# Revit family: QF_ELECTROLUXPROFESSIONAL_1LSN7U_WB6-35_E
name_source: partatom
category: Attrezzature speciali
units: mm (PartAtom-declared; Revit-internal decimal feet)

## family parameters
Basato su piano di lavoro = No
Condiviso = No
Punto di calcolo locali = No
Quota connettore circolare = Usa diametro
Sempre verticale = Sì
Taglio con vuoti quando caricato = No
Tipo di parte = Normale

## types (67) — shared parameters
Cold Water Maximum Pressure = 0.00 psi
Cold Water Minimum Pressure = 0.00 psi
Cold Water Size = 1"
Conn Conduit = Sì
Depth Actual = 1030 mm  [stored 3.37927 ft]
Electrical Remarks = 400 V/3N ph/50/60 Hz
Height Actual = 1620 mm
Hot Water Consumption = 0 GPM
Hot Water Maximum Pressure = 0.00 psi
Hot Water Minimum Pressure = 0.00 psi
Hot Water Size = 1"
Hot Water Temperature = -460 °F
Indirect Waste Size = 1"
Latent Heat Output = 0.0
Length Actual = 1270 mm  [stored 4.16667 ft]
Max Overcurrent Protection = 0 A
Min Ckt Ampacity = 0 A
Modello = WB6-35
Phase = 3
Produttore = Electrolux Professional
Sensible Heat Output = 0.0
URL = www.electroluxprofessional.com
Weight = 770
Weight in Pounds = 55.1
zero-valued in all types: Cold Water Connection Height, Gas KW, Hot Water Connection Height, Indirect Waste Connection Height, Prospetto di default, Steam Pounds per Hour

## per-type parameters (varying)
| type | Descrizione | Volts | Watts |
| 9890230074 | WASHER WB6-35 350L 2DOORS LEFT/LEFT EL. 380-415/50/60/3 COMPASS PRO 2xWATER 13xLIQ. SILVER EXP. | 415 V | 28800 W |
| 9890230044 | WASHER WB6-35 350L 2DOORS RIGHT/LEFT EL. 380-415/50/60/3 2xCOMPASS PRO 2xWATER 13xLIQ. SILVER ALARM | 415 V | 28800 W |
| 9890230034 | WASHER WB6-35 350L 2DOORS RIGHT/RIGHT EL. 380-415/50/60/3 COMPASS PRO 3xWATER 13xLIQ.+POWDER SILVER EXP. | 415 V | 28800 W |
| 9890230014 | WASHER WB6-35 350L 2DOORS RIGHT/RIGHT EL. 230/50/60/3 2xCOMPASS PRO 2xWATER 13xLIQ. SILVER AIDO TAP ALARM EXP. | 230 V | 28800 W |
| 9890230061 | WASHER WB6-35 350L 2DOORS RIGHT/RIGHT EL. 380-415/50/60/3 2xCOMPASS PRO 2xWATER 13xLIQ.+POWDER SST AIDO ALARM EXP. | 415 V | 31500 W |
| 9890230051 | WASHER WB6-35 350L 2DOORS RIGHT/RIGHT EL. 380-415/50/60/3 COMPASS PRO 2xWATER 13xLIQ. SILVER TAP ALARM EXP. | 415 V | 28800 W |
| 9890230041 | WASHER WB6-35 350L 2DOORS LEFT/RIGHT EL. 380-415/50/60/3 COMPASS PRO 3xWATER 13xLIQ.+POWDER SILVER EXP. | 415 V | 28800 W |
| 9890230031 | WASHER WB6-35 350L 2DOORS RIGHT/RIGHT EL. 380-415/50/60/3 2xCOMPASS PRO 2xWATER 13xLIQ. SILVER AIDO | 415 V | 28800 W |
| 9890230021 | WASHER WB6-35 350L 2DOORS RIGHT/RIGHT EL. 380-415/50/60/3 2xCOMPASS PRO 2xWATER 13xLIQ. SILVER EXP. | 415 V | 28800 W |
| 9890230011 | WASHER WB6-35 350L 2DOORS RIGHT/LEFT EL. 380-415/50/60/3 COMPASS PRO 2xWATER 13xLIQ. SILVER | 415 V | 28800 W |
| 9893230007 | WASHER WB6-35 350L 2DOORS RIGHT/RIGHT EL. 480/50/60/3 COMPASS PRO 2xWATER 13xLIQ. SILVER TAP ALARM EXP. ETL | 480 V | 28800 W |
| 9891230006 | WASHER WB6-35 350L 1DOOR RIGHT EL. 380-415/50/60/3 COMPASS PRO 2xWATER 13xLIQ. SILVER | 415 V | 28800 W |
| 9890230059 | WASHER WB6-35 350L 2DOORS LEFT/LEFT EL. 380-415/50/60/3 2xCOMPASS PRO 2xWATER 13xLIQ. SILVER TAP ALARM EXP. | 415 V | 28800 W |
| 9890230049 | WASHER WB6-35 350L 2DOORS LEFT/RIGHT EL. 380-415/50/60/3 2xCOMPASS PRO 2xWATER 13xLIQ. SILVER AIDO IWS ALARM | 415 V | 28800 W |
| 9890230039 | WASHER WB6-35 350L 2DOORS RIGHT/RIGHT EL. 380-415/50/60/3 2xCOMPASS PRO 2xWATER 13xLIQ. SILVER TAP ALARM | 415 V | 28800 W |
| 9890230029 | WASHER WB6-35 350L 2DOORS LEFT/RIGHT EL. 380-415/50/60/3 COMPASS PRO 3xWATER 13xLIQ. SILVER | 415 V | 28800 W |
| 9890230019 | WASHER WB6-35 350L 2DOORS RIGHT/RIGHT EL. 380-415/50/60/3 COMPASS PRO 2xWATER 13xLIQ. SILVER ALARM EXP. | 415 V | 28800 W |
| 9890230009 | WASHER WB6-35 350L 2DOORS RIGHT/RIGHT EL. 380-415/50/60/3 2xCOMPASS PRO 2xWATER 13xLIQ. SILVER IWS ALARM EXP. | 415 V | 28800 W |
| 9891230001 | WASHER WB6-35 350L 1DOOR RIGHT EL. 380-415/50/60/3 COMPASS PRO 2xWATER 13xLIQ.+POWDER SILVER | 415 V | 28800 W |
| 9893230002 | WASHER WB6-35 350L 2DOORS RIGHT/RIGHT EL. 208-240/50/60/3 2xCOMPASS PRO 3xWATER 13xLIQ. SILVER AIDO ALARM EXP. ETL | 240 V | 28800 W |
| 9890230052 | WASHER WB6-35 350L 2DOORS RIGHT/RIGHT EL. 380-415/50/60/3 2xCOMPASS PRO 2xWATER 13xLIQ.+POWDER SST ALARM EXP. | 415 V | 28800 W |
| 9890230022 | WASHER WB6-35 350L 2DOORS RIGHT/RIGHT EL. 380-415/50/60/3 2xCOMPASS PRO 2xWATER 13xLIQ.+POWDER SILVER EXP. | 415 V | 28800 W |
| 9890230012 | WASHER WB6-35 350L 2DOORS LEFT/RIGHT EL. 380-415/50/60/3 COMPASS PRO 2xWATER 13xLIQ. SILVER | 415 V | 28800 W |
| 9890230082 | WASHER WB6-35 350L 2DOORS RIGHT/RIGHT EL. 380-415/50/60/3 2xCOMPASS PRO 2xWATER 13xLIQ. SILVER ALARM BMP EXP. | 415 V | 28800 W |
| 9893230001 | WASHER WB6-35 350L 2DOORS RIGHT/RIGHT NO HEATING 208-240/50/60/3 COMPASS PRO 2xWATER 13xLIQ.+POWDER SST ALARM EXP. ETL | 240 V | 6400 W |
| 9890230067 | WASHER WB6-35 350L 2DOORS RIGHT/RIGHT EL. 380-415/50/60/3 2xCOMPASS PRO 2xWATER 13xLIQ. SILVER IWS EXP. | 415 V | 28800 W |
| 9890230057 | WASHER WB6-35 350L 2DOORS RIGHT/RIGHT EL. 380-415/50/60/3 COMPASS PRO 2xWATER 13xLIQ.+POWDER SILVER ALARM EXP. | 415 V | 28800 W |
| 9890230047 | WASHER WB6-35 350L 2DOORS RIGHT/RIGHT EL. 380-415/50/60/3 2xCOMPASS PRO 3xWATER 13xLIQ. SILVER ALARM | 415 V | 28800 W |
| 9890230027 | WASHER WB6-35 350L 2DOORS RIGHT/RIGHT EL. 380-415/50/60/3 COMPASS PRO 2xWATER 13xLIQ.+POWDER SST EXP. | 415 V | 28800 W |
| 9890230017 | WASHER WB6-35 350L 2DOORS LEFT/RIGHT EL. 380-415/50/60/3 COMPASS PRO 2xWATER 13xLIQ. SILVER ALARM | 415 V | 28800 W |
| 9890230007 | WASHER WB6-35 350L 2DOORS RIGHT/RIGHT EL. 380-415/50/60/3 2xCOMPASS PRO 2xWATER 13xLIQ. SILVER | 415 V | 28800 W |
| 9890230070 | WASHER WB6-35 350L 2DOORS RIGHT/RIGHT EL. 380-415/50/60/3 COMPASS PRO 2xWATER 13xLIQ.+POWDER SILVER EXP. | 415 V | 28800 W |
| 9890230060 | WASHER WB6-35 350L 2DOORS RIGHT/RIGHT EL. 380-415/50/60/3 2xCOMPASS PRO 2xWATER 13xLIQ. SILVER AIDO ALARM | 415 V | 31500 W |
| 9890230040 | WASHER WB6-35 350L 2DOORS LEFT/RIGHT EL. 380-415/50/60/3 COMPASS PRO 2xWATER 13xLIQ.+POWDER SILVER BMP | 415 V | 28800 W |
| 9890230030 | WASHER WB6-35 350L 2DOORS RIGHT/RIGHT EL. 380-415/50/60/3 COMPASS PRO 2xWATER 13xLIQ. SILVER IWS | 415 V | 28800 W |
| 9890230020 | WASHER WB6-35 350L 2DOORS RIGHT/RIGHT EL. 380-415/50/60/3 2xCOMPASS PRO 2xWATER 13xLIQ.+POWDER SILVER AIDO | 415 V | 28800 W |
| 9890230010 | WASHER WB6-35 350L 2DOORS RIGHT/RIGHT EL. 380-415/50/60/3 2xCOMPASS PRO 2xWATER 13xLIQ. SILVER AIDO IWS TAP ALARM EXP. | 415 V | 28800 W |
| 9893230004 | WASHER WB6-35 350L 2DOORS RIGHT/RIGHT EL. 208-240/50/60/3 COMPASS PRO 2xWATER 13xLIQ.+POWDER SILVER ALARM EXP. ETL | 240 V | 28800 W |
| 9890230078 | WASHER WB6-35 350L 2DOORS RIGHT/RIGHT EL. 380-415/50/60/3 2xCOMPASS PRO 2xWATER 13xLIQ. SILVER AIDO IWS TAP ALARM EXP. | 415 V | 28800 W |
| 9890230048 | WASHER WB6-35 350L 2DOORS LEFT/RIGHT EL. 380-415/50/60/3 COMPASS PRO 2xWATER 13xLIQ. SILVER EXP. | 415 V | 28800 W |
| 9890230038 | WASHER WB6-35 350L 2DOORS RIGHT/RIGHT EL. 380-415/50/60/3 2xCOMPASS PRO 2xWATER 13xLIQ.+POWDER SILVER | 415 V | 28800 W |
| 9890230028 | WASHER WB6-35 350L 2DOORS RIGHT/RIGHT EL. 380-415/50/60/3 COMPASS PRO 2xWATER 13xLIQ. SST IWS TAP ALARM EXP. | 415 V | 28800 W |
| 9890230018 | WASHER WB6-35 350L 2DOORS RIGHT/RIGHT EL. 380-415/50/60/3 2xCOMPASS PRO 2xWATER 13xLIQ. SILVER AIDO TAP ALARM | 415 V | 28800 W |
| 9890230008 | WASHER WB6-35 350L 2DOORS RIGHT/RIGHT EL. 380-415/50/60/3 COMPASS PRO 2xWATER 13xLIQ. SILVER | 415 V | 28800 W |
| 9890230080 | WASHER WB6-35 350L 2DOORS RIGHT/LEFT EL. 380-415/50/60/3 COMPASS PRO 2xWATER 13xLIQ. SILVER EXP. | 415 V | 28800 W |
| 9890230075 | WASHER WB6-35 350L 2DOORS RIGHT/RIGHT EL. 380-415/50/60/3 2xCOMPASS PRO 3xWATER 13xLIQ.+POWDER SILVER AIDO TAP ALARM | 415 V | 28800 W |
| 9893230003 | WASHER WB6-35 350L 2DOORS RIGHT/RIGHT NO HEATING 208-240/50/60/3 COMPASS PRO 2xWATER 13xLIQ.+POWDER SILVER ALARM EXP. ET | 240 V | 6400 W |
| 9890230065 | WASHER WB6-35 350L 2DOORS RIGHT/RIGHT EL. 380-415/50/60/3 COMPASS PRO 3xWATER 13xLIQ.+POWDER 2xDRAIN SILVER ALARM EXP. | 415 V | 28800 W |
| 9890230045 | WASHER WB6-35 350L 2DOORS LEFT/RIGHT EL. 380-415/50/60/3 COMPASS PRO 3xWATER 13xLIQ. SILVER EXP. | 415 V | 28800 W |
| 9890230035 | WASHER WB6-35 350L 2DOORS RIGHT/LEFT EL. 380-415/50/60/3 2xCOMPASS PRO 2xWATER 13xLIQ. SILVER IWS ALARM EXP. | 415 V | 28800 W |
| 9890230025 | WASHER WB6-35 350L 2DOORS RIGHT/RIGHT EL. 380-415/50/60/3 COMPASS PRO 2xWATER 13xLIQ.+POWDER SILVER BMP | 415 V | 28800 W |
| 9890230015 | WASHER WB6-35 350L 2DOORS RIGHT/RIGHT EL. 380-415/50/60/3 2xCOMPASS PRO 2xWATER 13xLIQ. SILVER TAP ALARM EXP. | 415 V | 28800 W |
| 9890230005 | WASHER WB6-35 350L 2DOORS RIGHT/RIGHT EL. 380-415/50/60/3 2xCOMPASS PRO 3xWATER 13xLIQ.+POWDER 2xDRAIN SILVER AIDO IWS T | 415 V | 28800 W |
| 9893230006 | WASHER WB6-35 350L 2DOORS RIGHT/RIGHT EL. 480/50/60/3 COMPASS PRO 2xWATER 13xLIQ.+POWDER SILVER TAP ALARM EXP. ETL | 480 V | 28800 W |
| 9891230005 | WASHER WB6-35 350L 1DOOR RIGHT NO HEATING 380-415/50/60/3 COMPASS PRO 3xWATER 13xLIQ.+POWDER 2xDRAIN SILVER | 415 V | 6400 W |
| 9890230076 | WASHER WB6-35 350L 2DOORS RIGHT/RIGHT EL. 380-415/50/60/3 2xCOMPASS PRO 2xWATER 13xLIQ. SILVER ALARM EXP. | 415 V | 28800 W |
| 9890230056 | WASHER WB6-35 350L 2DOORS LEFT/RIGHT EL. 380-415/50/60/3 2xCOMPASS PRO 2xWATER 13xLIQ. SILVER IWS BMP EXP. | 415 V | 28800 W |
| 9890230026 | WASHER WB6-35 350L 2DOORS RIGHT/RIGHT EL. 380-415/50/60/3 COMPASS PRO 2xWATER 13xLIQ.+POWDER SST IWS TAP ALARM EXP. | 415 V | 28800 W |
| 9890230016 | WASHER WB6-35 350L 2DOORS RIGHT/RIGHT EL. 380-415/50/60/3 2xCOMPASS PRO 2xWATER 13xLIQ. SILVER AIDO TAP ALARM EXP. | 415 V | 28800 W |
| 9890230006 | WASHER WB6-35 350L 2DOORS RIGHT/RIGHT EL. 380-415/50/60/3 COMPASS PRO 2xWATER 13xLIQ.+POWDER SILVER EXP. | 415 V | 28800 W |
| 9890230063 | WASHER WB6-35 350L 2DOORS RIGHT/RIGHT EL. 380-415/50/60/3 2xCOMPASS PRO 3xWATER 13xLIQ.+POWDER SILVER IWS ALARM BMP EXP. | 415 V | 31500 W |
| 9890230053 | WASHER WB6-35 350L 2DOORS RIGHT/RIGHT EL. 380-415/50/60/3 2xCOMPASS PRO 2xWATER 13xLIQ. SST ALARM EXP. | 415 V | 28800 W |
| 9890230043 | WASHER WB6-35 350L 2DOORS RIGHT/RIGHT EL. 380-415/50/60/3 2xCOMPASS PRO 2xWATER 13xLIQ. SILVER ALARM | 415 V | 28800 W |
| 9890230033 | WASHER WB6-35 350L 2DOORS RIGHT/RIGHT EL. 380-415/50/60/3 2xCOMPASS PRO 3xWATER 13xLIQ.+POWDER SILVER AIDO ALARM EXP. | 415 V | 28800 W |
| 9890230023 | WASHER WB6-35 350L 2DOORS RIGHT/RIGHT EL. 380-415/50/60/3 COMPASS PRO 2xWATER 13xLIQ.+POWDER SILVER EXP. | 415 V | 28800 W |
| 9890230013 | WASHER WB6-35 350L 2DOORS RIGHT/RIGHT EL. 230/50/60/3 2xCOMPASS PRO 2xWATER 13xLIQ. SILVER TAP ALARM EXP. | 230 V | 28800 W |
| 9890230083 | WASHER WB6-35 350L 2DOORS RIGHT/RIGHT NO HEATING 380-415/50/60/3 2xCOMPASS PRO 3xWATER 13xLIQ. SILVER AIDO ALARM | 415 V | 6400 W |

note: [stored X ft] marks values corroborated as IEEE doubles in the binary element streams (Revit-internal decimal feet)

## geometry (parser evidence)
native form markers: Blend x4, Sweep x3
no freeform markers — native parametric forms only
